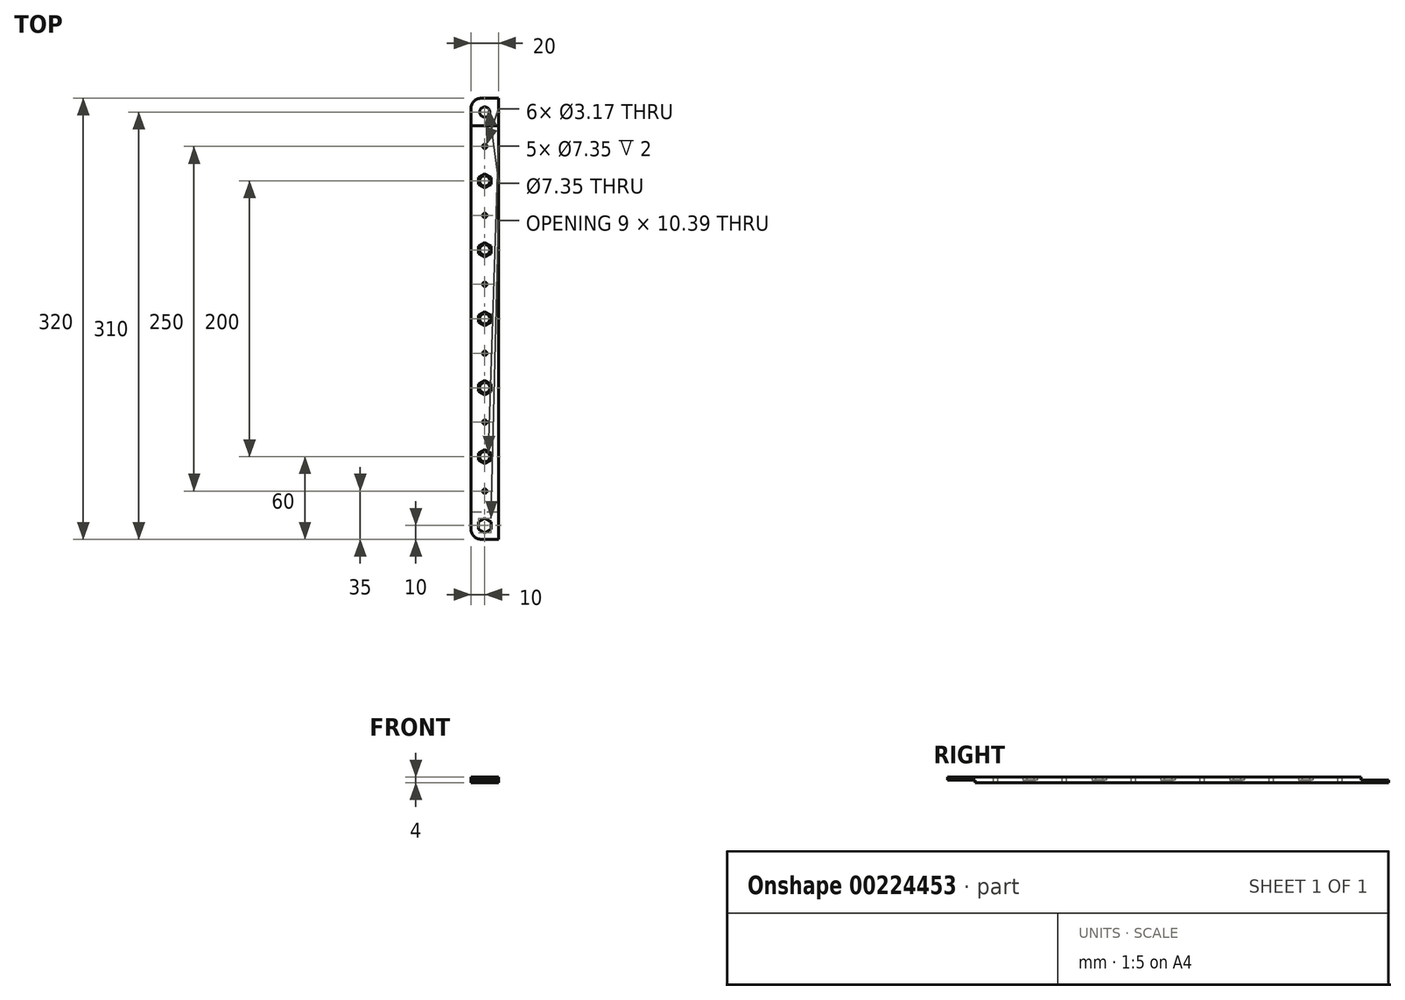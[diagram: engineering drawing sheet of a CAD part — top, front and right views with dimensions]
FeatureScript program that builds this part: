
annotation { "Feature Type Name" : "Feature", "Feature Type Description" : "" }
export const myFeature = defineFeature(function(context is Context, id is Id, definition is map)
    precondition{}
    {
        {
            var Q0;
            Q0=qCreatedBy(makeId("Top.planeOp"),FACE);
            var sketch = newSketch(context, id + "F0", { "sketchPlane" : qUnion([Q0])});
            skLineSegment(sketch, "E0.bottom", {"start": v(10, 160) * mm, "end": v(-2.5, 160) * mm});
            skLineSegment(sketch, "E0.top", {"start": v(10, -160) * mm, "end": v(-2.5, -160) * mm});
            skLineSegment(sketch, "E0.left", {"start": v(10, 160) * mm, "end": v(10, -160) * mm});
            skLineSegment(sketch, "E0.right", {"start": v(-10, 152.5) * mm, "end": v(-10, -152.5) * mm});
            skPoint(sketch, "E0.middle", {"position": v(0, 0) * mm});
            skLineSegment(sketch, "E1", {"start": v(0, 150) * mm, "end": v(0, 100) * mm, "construction": true});
            skLineSegment(sketch, "E2", {"start": v(0, 0) * mm, "end": v(0, -50) * mm, "construction": true});
            skLineSegment(sketch, "E3", {"start": v(0, 50) * mm, "end": v(0, 0) * mm, "construction": true});
            skLineSegment(sketch, "E4", {"start": v(0, 100) * mm, "end": v(0, 50) * mm, "construction": true});
            skLineSegment(sketch, "E5", {"start": v(0, -100) * mm, "end": v(0, -150) * mm, "construction": true});
            skLineSegment(sketch, "E6", {"start": v(0, -50) * mm, "end": v(0, -100) * mm, "construction": true});
            skPoint(sketch, "E7", {"position": v(0, 125) * mm});
            skPoint(sketch, "E8", {"position": v(0, 75) * mm});
            skPoint(sketch, "E9", {"position": v(0, 25) * mm});
            skPoint(sketch, "E10", {"position": v(0, -25) * mm});
            skPoint(sketch, "E11", {"position": v(0, -75) * mm});
            skPoint(sketch, "E12", {"position": v(0, -125) * mm});
            skCircle(sketch, "E13", {"center": v(0, 125) * mm, "radius": 1.59 * mm});
            skCircle(sketch, "E14", {"center": v(0, 75) * mm, "radius": 1.59 * mm});
            skCircle(sketch, "E15", {"center": v(0, 25) * mm, "radius": 1.59 * mm});
            skCircle(sketch, "E16", {"center": v(0, -25) * mm, "radius": 1.59 * mm});
            skCircle(sketch, "E17", {"center": v(0, -75) * mm, "radius": 1.59 * mm});
            skCircle(sketch, "E18", {"center": v(0, -125) * mm, "radius": 1.59 * mm});
            skCircle(sketch, "E19", {"center": v(0, 150) * mm, "radius": 3.68 * mm});
            skCircle(sketch, "E20", {"center": v(0, 100) * mm, "radius": 3.68 * mm});
            skCircle(sketch, "E21", {"center": v(0, 50) * mm, "radius": 3.68 * mm});
            skCircle(sketch, "E22", {"center": v(0, 0) * mm, "radius": 3.68 * mm});
            skCircle(sketch, "E23", {"center": v(0, -50) * mm, "radius": 3.68 * mm});
            skCircle(sketch, "E24", {"center": v(0, -100) * mm, "radius": 3.68 * mm});
            skCircle(sketch, "E25", {"center": v(0, -150) * mm, "radius": 3.68 * mm});
            skCircle(sketch, "E26.cCircle", {"center": v(0, 150) * mm, "radius": 4.5 * mm, "construction": true});
            skLineSegment(sketch, "E26.0", {"start": v(-4.5, 147.4) * mm, "end": v(-4.5, 152.6) * mm});
            skLineSegment(sketch, "E26.1", {"start": v(-4.5, 152.6) * mm, "end": v(0, 155.2) * mm});
            skLineSegment(sketch, "E26.2", {"start": v(0, 155.2) * mm, "end": v(4.5, 152.6) * mm});
            skLineSegment(sketch, "E26.3", {"start": v(4.5, 152.6) * mm, "end": v(4.5, 147.4) * mm});
            skLineSegment(sketch, "E26.4", {"start": v(4.5, 147.4) * mm, "end": v(0, 144.8) * mm});
            skLineSegment(sketch, "E26.5", {"start": v(0, 144.8) * mm, "end": v(-4.5, 147.4) * mm});
            skPoint(sketch, "E26.0.midPoint", {"position": v(-4.5, 150) * mm});
            skCircle(sketch, "E27.cCircle", {"center": v(0, 100) * mm, "radius": 4.5 * mm, "construction": true});
            skLineSegment(sketch, "E27.0", {"start": v(-4.5, 97.4) * mm, "end": v(-4.5, 102.6) * mm});
            skLineSegment(sketch, "E27.1", {"start": v(-4.5, 102.6) * mm, "end": v(0, 105.2) * mm});
            skLineSegment(sketch, "E27.2", {"start": v(0, 105.2) * mm, "end": v(4.5, 102.6) * mm});
            skLineSegment(sketch, "E27.3", {"start": v(4.5, 102.6) * mm, "end": v(4.5, 97.4) * mm});
            skLineSegment(sketch, "E27.4", {"start": v(4.5, 97.4) * mm, "end": v(0, 94.8) * mm});
            skLineSegment(sketch, "E27.5", {"start": v(0, 94.8) * mm, "end": v(-4.5, 97.4) * mm});
            skPoint(sketch, "E27.0.midPoint", {"position": v(-4.5, 100) * mm});
            skCircle(sketch, "E28.cCircle", {"center": v(0, 50) * mm, "radius": 4.5 * mm, "construction": true});
            skLineSegment(sketch, "E28.0", {"start": v(-4.5, 47.4) * mm, "end": v(-4.5, 52.6) * mm});
            skLineSegment(sketch, "E28.1", {"start": v(-4.5, 52.6) * mm, "end": v(0, 55.2) * mm});
            skLineSegment(sketch, "E28.2", {"start": v(0, 55.2) * mm, "end": v(4.5, 52.6) * mm});
            skLineSegment(sketch, "E28.3", {"start": v(4.5, 52.6) * mm, "end": v(4.5, 47.4) * mm});
            skLineSegment(sketch, "E28.4", {"start": v(4.5, 47.4) * mm, "end": v(0, 44.8) * mm});
            skLineSegment(sketch, "E28.5", {"start": v(0, 44.8) * mm, "end": v(-4.5, 47.4) * mm});
            skPoint(sketch, "E28.0.midPoint", {"position": v(-4.5, 50) * mm});
            skCircle(sketch, "E29.cCircle", {"center": v(0, 0) * mm, "radius": 4.5 * mm, "construction": true});
            skLineSegment(sketch, "E29.0", {"start": v(-4.5, -2.6) * mm, "end": v(-4.5, 2.6) * mm});
            skLineSegment(sketch, "E29.1", {"start": v(-4.5, 2.6) * mm, "end": v(0, 5.2) * mm});
            skLineSegment(sketch, "E29.2", {"start": v(0, 5.2) * mm, "end": v(4.5, 2.6) * mm});
            skLineSegment(sketch, "E29.3", {"start": v(4.5, 2.6) * mm, "end": v(4.5, -2.6) * mm});
            skLineSegment(sketch, "E29.4", {"start": v(4.5, -2.6) * mm, "end": v(0, -5.2) * mm});
            skLineSegment(sketch, "E29.5", {"start": v(0, -5.2) * mm, "end": v(-4.5, -2.6) * mm});
            skPoint(sketch, "E29.0.midPoint", {"position": v(-4.5, 0) * mm});
            skCircle(sketch, "E30.cCircle", {"center": v(0, -50) * mm, "radius": 4.5 * mm, "construction": true});
            skLineSegment(sketch, "E30.0", {"start": v(-4.5, -52.6) * mm, "end": v(-4.5, -47.4) * mm});
            skLineSegment(sketch, "E30.1", {"start": v(-4.5, -47.4) * mm, "end": v(0, -44.8) * mm});
            skLineSegment(sketch, "E30.2", {"start": v(0, -44.8) * mm, "end": v(4.5, -47.4) * mm});
            skLineSegment(sketch, "E30.3", {"start": v(4.5, -47.4) * mm, "end": v(4.5, -52.6) * mm});
            skLineSegment(sketch, "E30.4", {"start": v(4.5, -52.6) * mm, "end": v(0, -55.2) * mm});
            skLineSegment(sketch, "E30.5", {"start": v(0, -55.2) * mm, "end": v(-4.5, -52.6) * mm});
            skPoint(sketch, "E30.0.midPoint", {"position": v(-4.5, -50) * mm});
            skCircle(sketch, "E31.cCircle", {"center": v(0, -100) * mm, "radius": 4.5 * mm, "construction": true});
            skLineSegment(sketch, "E31.0", {"start": v(-4.5, -102.6) * mm, "end": v(-4.5, -97.4) * mm});
            skLineSegment(sketch, "E31.1", {"start": v(-4.5, -97.4) * mm, "end": v(0, -94.8) * mm});
            skLineSegment(sketch, "E31.2", {"start": v(0, -94.8) * mm, "end": v(4.5, -97.4) * mm});
            skLineSegment(sketch, "E31.3", {"start": v(4.5, -97.4) * mm, "end": v(4.5, -102.6) * mm});
            skLineSegment(sketch, "E31.4", {"start": v(4.5, -102.6) * mm, "end": v(0, -105.2) * mm});
            skLineSegment(sketch, "E31.5", {"start": v(0, -105.2) * mm, "end": v(-4.5, -102.6) * mm});
            skPoint(sketch, "E31.0.midPoint", {"position": v(-4.5, -100) * mm});
            skCircle(sketch, "E32.cCircle", {"center": v(0, -150) * mm, "radius": 4.5 * mm, "construction": true});
            skLineSegment(sketch, "E32.0", {"start": v(-4.5, -152.6) * mm, "end": v(-4.5, -147.4) * mm});
            skLineSegment(sketch, "E32.1", {"start": v(-4.5, -147.4) * mm, "end": v(0, -144.8) * mm});
            skLineSegment(sketch, "E32.2", {"start": v(0, -144.8) * mm, "end": v(4.5, -147.4) * mm});
            skLineSegment(sketch, "E32.3", {"start": v(4.5, -147.4) * mm, "end": v(4.5, -152.6) * mm});
            skLineSegment(sketch, "E32.4", {"start": v(4.5, -152.6) * mm, "end": v(0, -155.2) * mm});
            skLineSegment(sketch, "E32.5", {"start": v(0, -155.2) * mm, "end": v(-4.5, -152.6) * mm});
            skPoint(sketch, "E32.0.midPoint", {"position": v(-4.5, -150) * mm});
            skPoint(sketch, "E33.visualSharp", {"position": v(-10, 160) * mm});
            skArc(sketch, "E33.filletArc", {"start": v(-2.5, 160) * mm, "mid": v(-7.8, 157.8) * mm, "end": v(-10, 152.5) * mm});
            skPoint(sketch, "E34.visualSharp", {"position": v(-10, -160) * mm});
            skArc(sketch, "E34.filletArc", {"start": v(-10, -152.5) * mm, "mid": v(-7.8, -157.8) * mm, "end": v(-2.5, -160) * mm});
            skLineSegment(sketch, "E35", {"start": v(-10, -140) * mm, "end": v(10, -140) * mm});
            skLineSegment(sketch, "E36", {"start": v(-10, 140) * mm, "end": v(10, 140) * mm});
            skSolve(sketch);
        }
        {
            var Q0;
            Q0=makeQuery(id+"F0.imprint","IMPRINT",FACE,{"disambiguationData":[TD([[makeQuery(id+"F0.imprint","IMPRINT",EDGE,{"derivedFrom":sQuery(id+"F0.wireOp",EDGE,"E13")}),-1.0]])]});
            var Q1;
            {var subQ1=sQuery(id+"F0.wireOp",EDGE,"E0.bottom");Q1=makeQuery(id+"F0.imprint","IMPRINT",FACE,{"disambiguationData":[TD([[makeQuery(id+"F0.imprint","IMPRINT",EDGE,{"derivedFrom":subQ1}),1.0]])]});}
            var Q2;
            Q2=makeQuery(id+"F0.imprint","IMPRINT",FACE,{"disambiguationData":[TD([[makeQuery(id+"F0.imprint","IMPRINT",EDGE,{"derivedFrom":sQuery(id+"F0.wireOp",EDGE,"E24")}),-1.0]])]});
            var Q3;
            Q3=makeQuery(id+"F0.imprint","IMPRINT",FACE,{"disambiguationData":[TD([[makeQuery(id+"F0.imprint","IMPRINT",EDGE,{"derivedFrom":sQuery(id+"F0.wireOp",EDGE,"E23")}),-1.0]])]});
            var Q4;
            Q4=makeQuery(id+"F0.imprint","IMPRINT",FACE,{"disambiguationData":[TD([[makeQuery(id+"F0.imprint","IMPRINT",EDGE,{"derivedFrom":sQuery(id+"F0.wireOp",EDGE,"E22")}),-1.0]])]});
            var Q5;
            Q5=makeQuery(id+"F0.imprint","IMPRINT",FACE,{"disambiguationData":[TD([[makeQuery(id+"F0.imprint","IMPRINT",EDGE,{"derivedFrom":sQuery(id+"F0.wireOp",EDGE,"E21")}),-1.0]])]});
            var Q6;
            Q6=makeQuery(id+"F0.imprint","IMPRINT",FACE,{"disambiguationData":[TD([[makeQuery(id+"F0.imprint","IMPRINT",EDGE,{"derivedFrom":sQuery(id+"F0.wireOp",EDGE,"E20")}),-1.0]])]});
            var Q7;
            Q7=makeQuery(id+"F0.imprint","IMPRINT",FACE,{"disambiguationData":[TD([[makeQuery(id+"F0.imprint","IMPRINT",EDGE,{"derivedFrom":sQuery(id+"F0.wireOp",EDGE,"E19")}),-1.0]])]});
            extrude(context, id + "F1", {"entities" : qUnion([Q0, Q1, Q2, Q3, Q4, Q5, Q6, Q7]), "oppositeDirection" : true, "depth" : 2 * mm});
        }
        {
            var Q0;
            Q0=makeQuery(id+"F0.imprint","IMPRINT",FACE,{"disambiguationData":[TD([[makeQuery(id+"F0.imprint","IMPRINT",EDGE,{"derivedFrom":sQuery(id+"F0.wireOp",EDGE,"E13")}),-1.0]])]});
            var Q1;
            {var subQ1=sQuery(id+"F0.wireOp",EDGE,"E0.top");Q1=makeQuery(id+"F0.imprint","IMPRINT",FACE,{"disambiguationData":[TD([[makeQuery(id+"F0.imprint","IMPRINT",EDGE,{"derivedFrom":subQ1}),-1.0]])]});}
            extrude(context, id + "F2", {"entities" : qUnion([Q0, Q1]), "operationType" : NewBodyOperationType.ADD, "depth" : 2 * mm});
        }
    });
